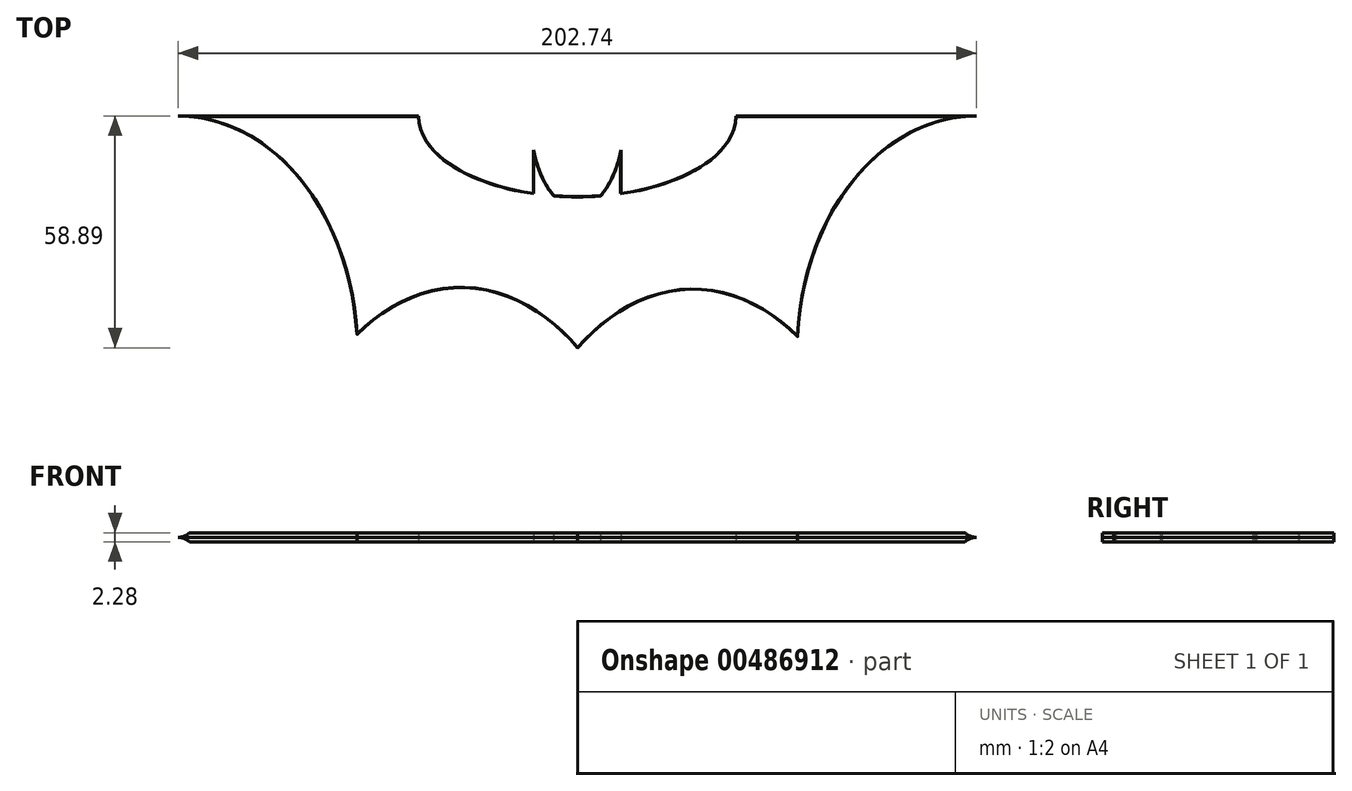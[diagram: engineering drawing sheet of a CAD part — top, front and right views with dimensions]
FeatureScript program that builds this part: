
annotation { "Feature Type Name" : "Feature", "Feature Type Description" : "" }
export const myFeature = defineFeature(function(context is Context, id is Id, definition is map)
    precondition{}
    {
        {
            var Q0;
            Q0=qCreatedBy(makeId("Top.planeOp"),FACE);
            var sketch = newSketch(context, id + "F0", { "sketchPlane" : qUnion([Q0])});
            skLineSegment(sketch, "E0.bottom", {"start": v(101.37, 59.86) * mm, "end": v(-101.37, 59.86) * mm});
            skLineSegment(sketch, "E0.top", {"start": v(101.37, -59.86) * mm, "end": v(-101.37, -59.86) * mm});
            skLineSegment(sketch, "E0.left", {"start": v(101.37, 59.86) * mm, "end": v(101.37, -59.86) * mm});
            skLineSegment(sketch, "E0.right", {"start": v(-101.37, 59.86) * mm, "end": v(-101.37, -59.86) * mm});
            skPoint(sketch, "E0.middle", {"position": v(0, 0) * mm});
            skEllipse(sketch, "E1", {"center": v(0, 59.86) * mm, "majorRadius": 40.3 * mm, "minorRadius": 20.46 * mm, "majorAxis": v(-1, 0)});
            skEllipse(sketch, "E2", {"center": v(-101.37, 0) * mm, "majorRadius": 59.86 * mm, "minorRadius": 45.5 * mm, "majorAxis": v(0, 1)});
            skEllipse(sketch, "E3", {"center": v(101.37, 0) * mm, "majorRadius": 59.86 * mm, "minorRadius": 45.5 * mm, "majorAxis": v(0, 1)});
            skEllipse(sketch, "E4", {"center": v(-29.5, -59.86) * mm, "majorRadius": 76.13 * mm, "minorRadius": 49.24 * mm, "majorAxis": v(0, 1)});
            skEllipse(sketch, "E5", {"center": v(29.38, -60.26) * mm, "majorRadius": 76.13 * mm, "minorRadius": 49.24 * mm, "majorAxis": v(0, 1)});
            skLineSegment(sketch, "E6.bottom", {"start": v(-11.1, 59.86) * mm, "end": v(11.1, 59.86) * mm});
            skLineSegment(sketch, "E6.top", {"start": v(-11.1, 27.23) * mm, "end": v(11.1, 27.23) * mm});
            skLineSegment(sketch, "E6.left", {"start": v(-11.1, 59.86) * mm, "end": v(-11.1, 27.23) * mm});
            skLineSegment(sketch, "E6.right", {"start": v(11.1, 59.86) * mm, "end": v(11.1, 27.23) * mm});
            skEllipse(sketch, "E7", {"center": v(0, 59.86) * mm, "majorRadius": 23.23 * mm, "minorRadius": 11.96 * mm, "majorAxis": v(0, -1)});
            skSolve(sketch);
        }
        {
            var Q0;
            {var subQ0=sQuery(id+"F0.wireOp",EDGE,"E6.left");var subQ1=sQuery(id+"F0.wireOp",EDGE,"E1");var subQ2=makeQuery(id+"F0.imprint","INTERSECT",VERTEX,{"derivedFrom":[subQ1,subQ0]});Q0=makeQuery(id+"F0.imprint","IMPRINT",FACE,{"disambiguationData":[TD([[makeQuery(id+"F0.imprint","IMPRINT",EDGE,{"disambiguationData":[TD([[subQ2,-1.0]])],"derivedFrom":subQ1}),1.0]])]});}
            var Q1;
            {var subQ0=sQuery(id+"F0.wireOp",EDGE,"E7");var subQ1=sQuery(id+"F0.wireOp",EDGE,"E1");var subQ2=makeQuery(id+"F0.imprint","INTERSECT",VERTEX,{"disambiguationData":[OD(3.0)],"derivedFrom":[subQ1,subQ0]});Q1=makeQuery(id+"F0.imprint","IMPRINT",FACE,{"disambiguationData":[TD([[makeQuery(id+"F0.imprint","IMPRINT",EDGE,{"disambiguationData":[TD([[subQ2,-1.0]])],"derivedFrom":subQ1}),1.0]])]});}
            var Q2;
            {var subQ0=sQuery(id+"F0.wireOp",EDGE,"E7");var subQ1=sQuery(id+"F0.wireOp",EDGE,"E1");var subQ2=makeQuery(id+"F0.imprint","INTERSECT",VERTEX,{"disambiguationData":[OD(2.0)],"derivedFrom":[subQ1,subQ0]});Q2=makeQuery(id+"F0.imprint","IMPRINT",FACE,{"disambiguationData":[TD([[makeQuery(id+"F0.imprint","IMPRINT",EDGE,{"disambiguationData":[TD([[subQ2,-1.0]])],"derivedFrom":subQ1}),-1.0]])]});}
            var Q3;
            {var subQ1=sQuery(id+"F0.wireOp",EDGE,"E6.top");Q3=makeQuery(id+"F0.imprint","IMPRINT",FACE,{"disambiguationData":[TD([[makeQuery(id+"F0.imprint","IMPRINT",EDGE,{"derivedFrom":subQ1}),1.0]])]});}
            var Q4;
            {var subQ0=sQuery(id+"F0.wireOp",EDGE,"E6.top");Q4=makeQuery(id+"F0.imprint","IMPRINT",FACE,{"disambiguationData":[TD([[makeQuery(id+"F0.imprint","IMPRINT",EDGE,{"derivedFrom":subQ0}),-1.0]])]});}
            extrude(context, id + "F1", {"entities" : qUnion([Q0, Q1, Q2, Q3, Q4]), "endBound" : BoundingType.SYMMETRIC, "depth" : 2.3 * mm, "hasDraft" : true, "draftAngle" : 3 * degree, "draftPullDirection" : true});
        }
    });
